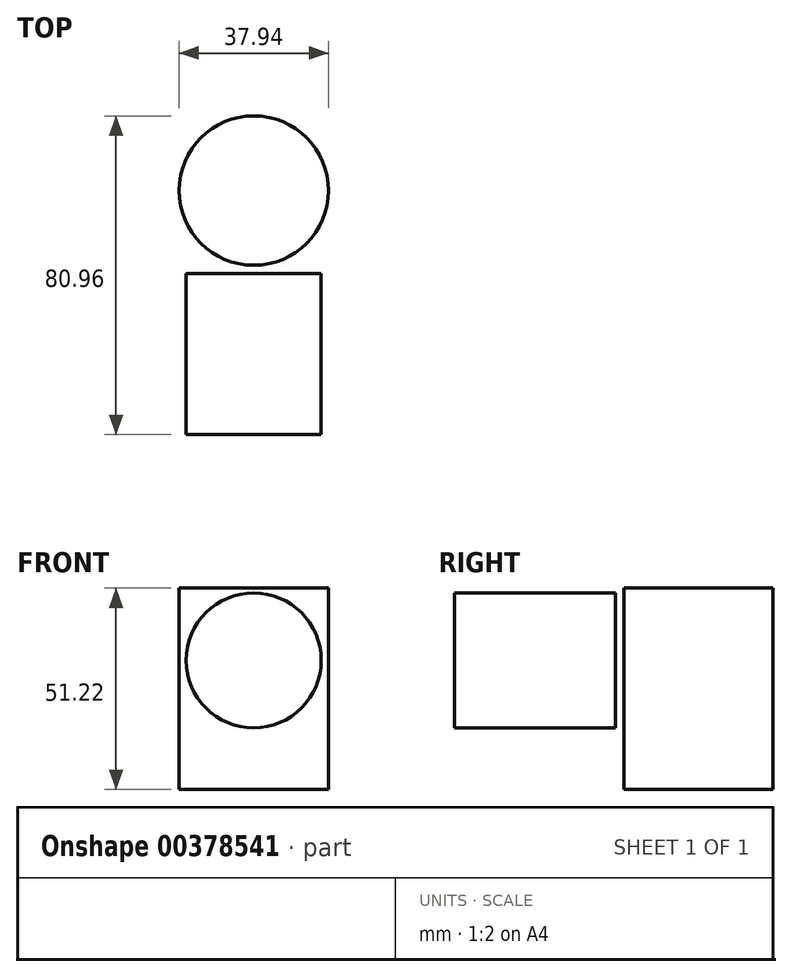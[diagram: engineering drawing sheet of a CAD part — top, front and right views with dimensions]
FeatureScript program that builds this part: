
annotation { "Feature Type Name" : "Feature", "Feature Type Description" : "" }
export const myFeature = defineFeature(function(context is Context, id is Id, definition is map)
    precondition{}
    {
        {
            var Q0;
            Q0=qCreatedBy(makeId("Front.planeOp"),FACE);
            var sketch = newSketch(context, id + "F0", { "sketchPlane" : qUnion([Q0])});
            skCircle(sketch, "E0", {"center": v(21.14, 32.83) * mm, "radius": 17.15 * mm});
            skSolve(sketch);
        }
        {
            var Q0;
            Q0 = qSketchRegion(id + "F0", true);
            extrude(context, id + "F1", {"entities" : qUnion([Q0]), "depth" : 40.94 * mm});
        }
        {
            var Q0;
            Q0=qCreatedBy(makeId("Top.planeOp"),FACE);
            var sketch = newSketch(context, id + "F2", { "sketchPlane" : qUnion([Q0])});
            skCircle(sketch, "E1", {"center": v(21.17, 21.05) * mm, "radius": 18.97 * mm});
            skSolve(sketch);
        }
        {
            var Q0;
            Q0=makeQuery(id+"F2.imprint","IMPRINT",FACE,{"disambiguationData":[TD([[makeQuery(id+"F2.imprint","IMPRINT",EDGE,{"derivedFrom":sQuery(id+"F2.wireOp",EDGE,"E1")}),1.0]])]});
            extrude(context, id + "F3", {"entities" : qUnion([Q0]), "depth" : 51.22 * mm});
        }
    });
